FCSTD DOCUMENT  (FreeCAD 1.0R38806 (Git))
Label: barras-simetricas
License: All rights reserved
LicenseURL: https://en.wikipedia.org/wiki/All_rights_reserved
objects: Sketcher::SketchObject×2, PartDesign::Body×1
note: 5 computed .brp shape members not serialized (recipe doc carries the construction recipe); baked Part::Feature solids carry a one-line shape summary decoded from their .brp

FEATURE [Sketcher::SketchObject] Sketch
  ArcFitTolerance = 1e-06
  AttachmentSupport = -> [XY_Plane]
  FullyConstrained = false
  MakeInternals = false
  MapMode = 5
  sketch-geometry (3):
    g0: LineSegment StartX=0 StartY=121.61 StartZ=0 EndX=0 EndY=0 EndZ=0
    g1: LineSegment StartX=0 StartY=0 StartZ=0 EndX=69.261 EndY=0 EndZ=0
    g2: LineSegment StartX=69.261 StartY=0 StartZ=0 EndX=18.0511 EndY=124.143 EndZ=0
  constraints (5):
    c: PointOnObject(g0,g-2)
    c: Coincident(g0,g-1)
    c: Coincident(g0,g1)
    c: PointOnObject(g1,g-1)
    c: Coincident(g1,g2)
FEATURE [Sketcher::SketchObject] Sketch001
  ArcFitTolerance = 1e-06
  AttachmentSupport = -> [XY_Plane]
  FullyConstrained = false
  MakeInternals = false
  MapMode = 5
  sketch-geometry (4):
    g0: LineSegment StartX=-36.565 StartY=0 StartZ=0 EndX=0 EndY=0 EndZ=0
    g1: LineSegment StartX=0 StartY=0 StartZ=0 EndX=36.565 EndY=0 EndZ=0
    g2: LineSegment StartX=-36.565 StartY=0 StartZ=0 EndX=-36.8762 EndY=111.43 EndZ=0
    g3: LineSegment StartX=36.565 StartY=0 StartZ=0 EndX=36.8762 EndY=111.43 EndZ=0
  constraints (11):
    c: PointOnObject(g0,g-1)
    c: Coincident(g0,g-1)
    c: Coincident(g1,g0)
    c: PointOnObject(g1,g-1)
    c: Block(g1)
    c: Block(g0)
    c: Coincident(g2,g0)
    c: Distance(g3) = 111.43
    c: Coincident(g3,g1)
    c: Distance(g2,g2) = 111.43
    c: Symmetric(g3,g2,g-2)
FEATURE [PartDesign::Body] Body
  AllowCompound = false
  Group = -> [Sketch,Sketch001]
  Origin = -> Origin
